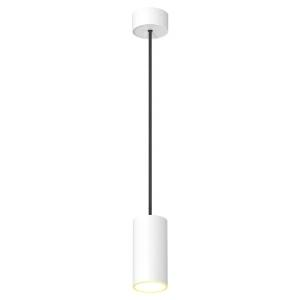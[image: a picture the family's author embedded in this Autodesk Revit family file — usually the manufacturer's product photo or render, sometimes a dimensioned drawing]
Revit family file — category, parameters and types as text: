
# Revit family: hangover_810-0490-h30-k18
name_source: partatom
category: Leuchten
revit_build: Autodesk Revit 2018 (Build: 20190510_1515(x64)
units: mm (PartAtom-declared; Revit-internal decimal feet)

## family parameters
Basisbauteil = Fläche
Beim Laden mit Abzugskörper schneiden = Nein
Bemaßung runder Anschluss = Durchmesser verwenden
Gemeinsam genutzt = Nein
Lichtquelle = Nein
Raumberechnungspunkt = Nein
Teiletyp = Normal

## types (1)
- 810-0490-H30-K18
    Beschreibung = HANGOVER
    CIE Flux Codes = 90 97 99 100 88
    Color Rendering = 1A/90…99
    Color Temperature = 3000K
    Height = 150 mm
    Hersteller = Prolicht
    Lamp Light Flux = 967
    Lamp Power = 9.8 W
    Lamp count = 1
    Lampe = 1 x LED
    Length = 75 mm
    Luminous efficacy = 87 lm/W
    ModVariant = Nein
    Modell = 810-0490-h30-k18-l00
    Mounting Place = Ceiling
    Mounting Type = Pendant
    Number of Poles = 1
    OnlyDefault = Ja
    Power Factor = 1
    Product Name = HANGOVER
    Product group = Suspended spotlights
    ProductGroupID = 942
    Protection Class = Protection class
    Protection Degree = Degree of protection
    RLX_Detail_Level = 1
    Scheinlast = 10 VA
    Socket = socket
    Standby Power = 0 W
    System Light Flux = 857 lm
    System Power = 10 W
    Typenbild = 410-7550.jpg
    Typenkommentare = LED COLOUR DIR 2700 K (27),REFLECTOR 18° (18),SHINE RING ABSICHTLICH_LEER (00)
    URL = http://prolicht.at
    VarID = 810-0470-h30-k18-l00
    Voltage = 0 V
    Vorgabe-Ansicht = 1800 mm
    Weight = 0.00 kg
    Width = 0 mm  [stored 0 ft]

note: [stored X ft] marks values corroborated as IEEE doubles in the binary element streams (Revit-internal decimal feet)

## geometry (parser evidence)
native form markers: Sweep x10
no freeform markers — native parametric forms only
